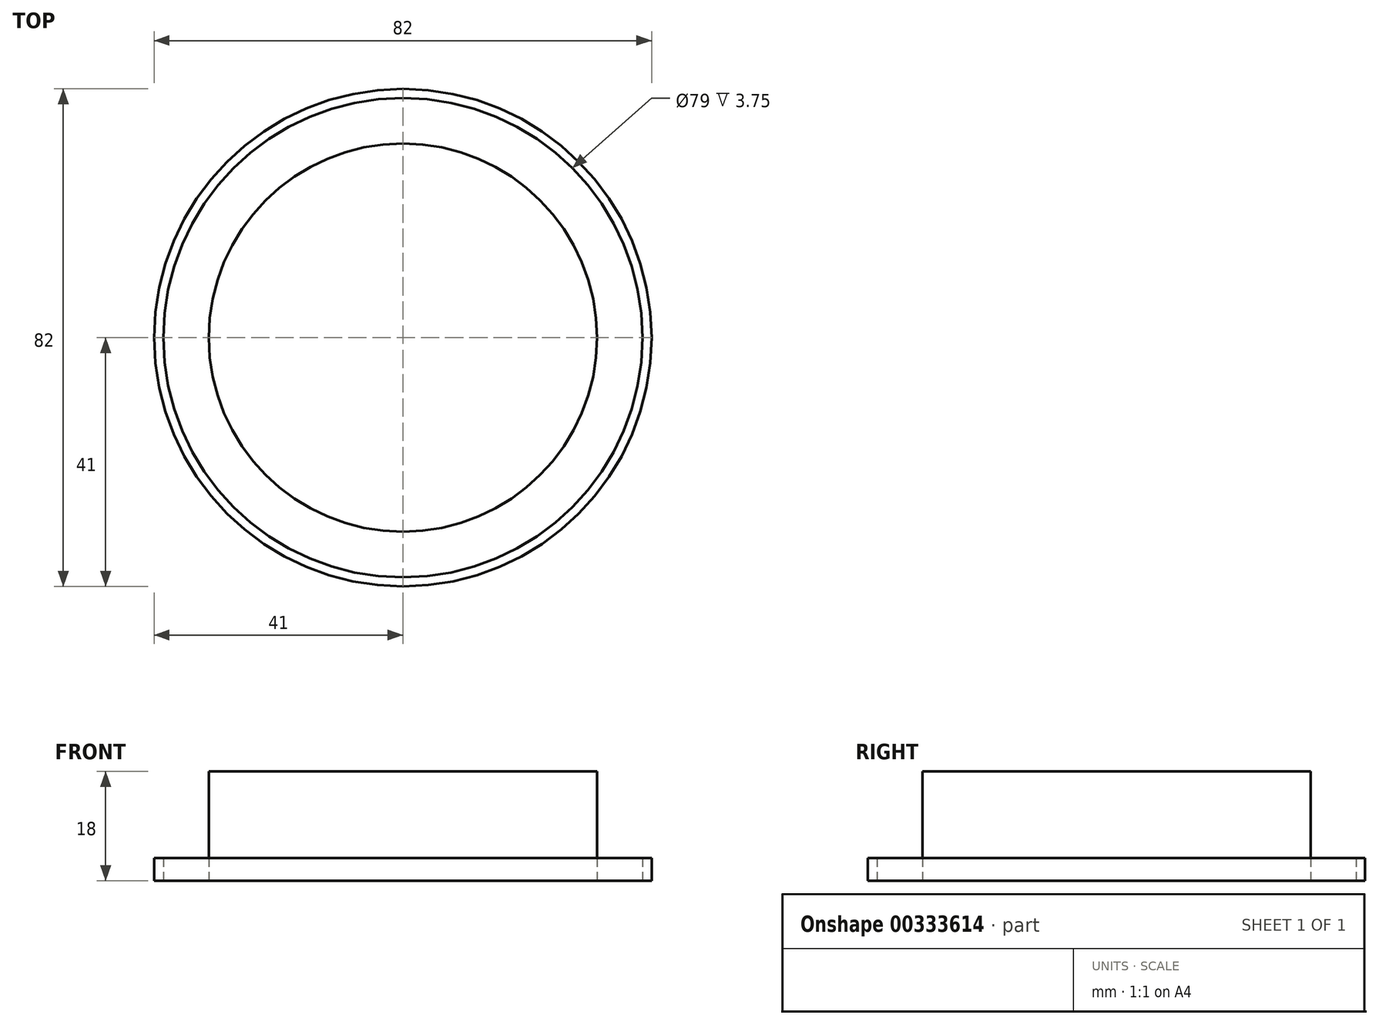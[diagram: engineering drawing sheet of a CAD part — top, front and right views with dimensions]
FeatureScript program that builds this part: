
annotation { "Feature Type Name" : "Feature", "Feature Type Description" : "" }
export const myFeature = defineFeature(function(context is Context, id is Id, definition is map)
    precondition{}
    {
        {
            var Q0;
            Q0=qCreatedBy(makeId("Top.planeOp"),FACE);
            var sketch = newSketch(context, id + "F0", { "sketchPlane" : qUnion([Q0])});
            skCircle(sketch, "E0", {"center": v(0, 0) * mm, "radius": 41 * mm});
            skCircle(sketch, "E1", {"center": v(0, 0) * mm, "radius": 39.5 * mm});
            skSolve(sketch);
        }
        {
            var Q0;
            Q0=makeQuery(id+"F0.imprint","IMPRINT",FACE,{"disambiguationData":[TD([[makeQuery(id+"F0.imprint","IMPRINT",EDGE,{"derivedFrom":sQuery(id+"F0.wireOp",EDGE,"E0")}),1.0]])]});
            extrude(context, id + "F1", {"entities" : qUnion([Q0]), "depth" : 3.75 * mm});
        }
        {
            var Q0;
            Q0=qCreatedBy(makeId("Top.planeOp"),FACE);
            var sketch = newSketch(context, id + "F2", { "sketchPlane" : qUnion([Q0])});
            skCircle(sketch, "E2", {"center": v(0, 0) * mm, "radius": 32 * mm});
            skSolve(sketch);
        }
        {
            var Q0;
            Q0 = qSketchRegion(id + "F2", true);
            var Q1;
            Q1=makeQuery(id+"F2.imprint","IMPRINT",FACE,{"disambiguationData":[TD([[makeQuery(id+"F2.imprint","IMPRINT",EDGE,{"derivedFrom":sQuery(id+"F2.wireOp",EDGE,"E2")}),1.0]])]});
            extrude(context, id + "F3", {"entities" : qUnion([Q0, Q1]), "depth" : 18 * mm});
        }
    });
